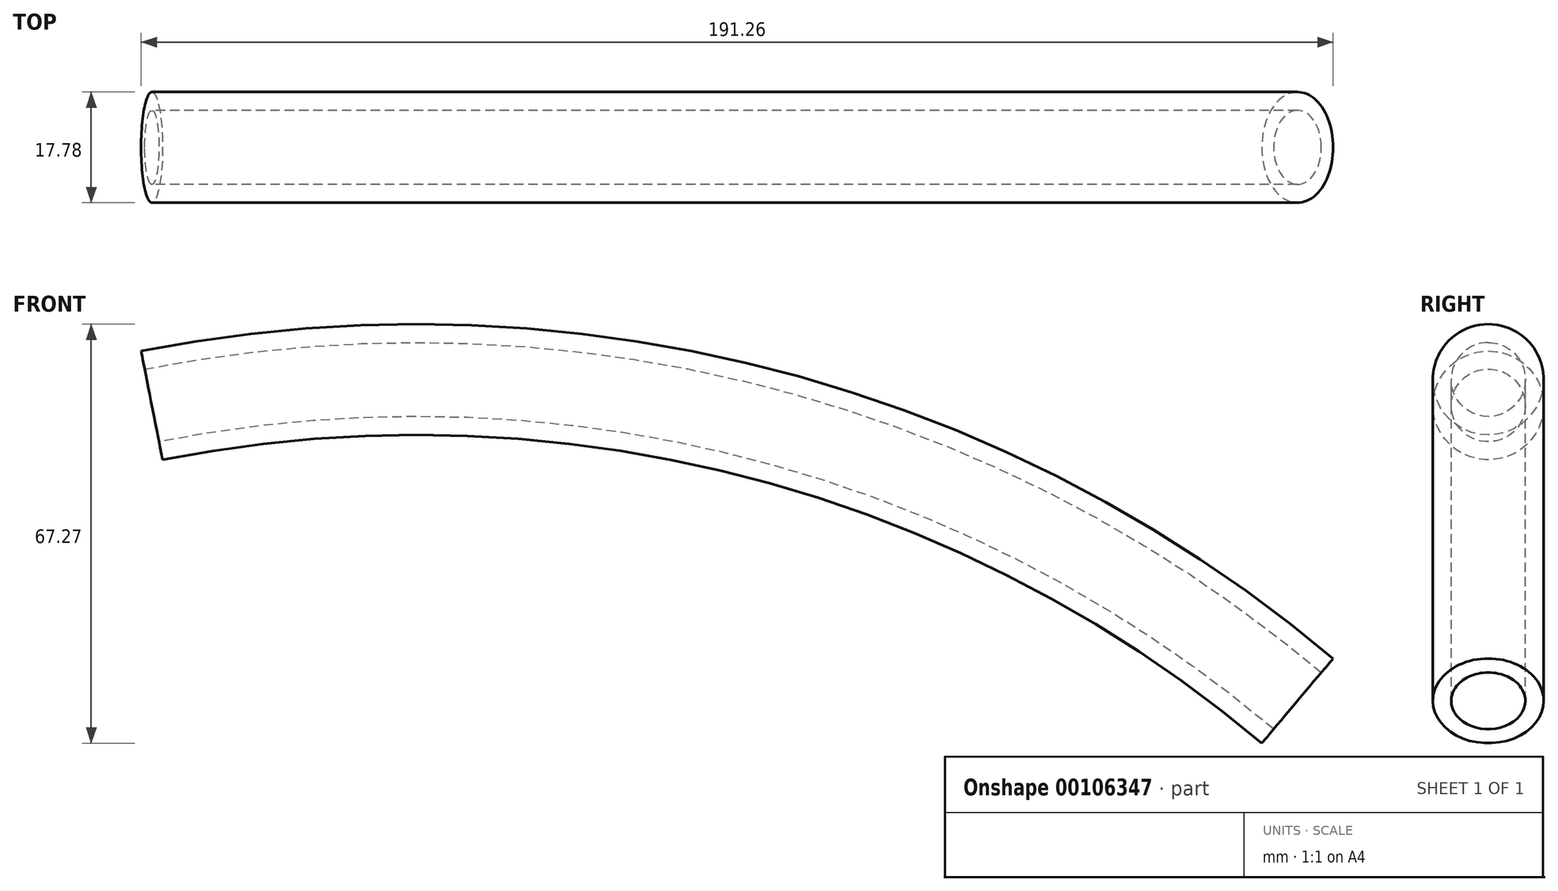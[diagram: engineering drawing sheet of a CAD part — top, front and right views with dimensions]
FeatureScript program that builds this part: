
annotation { "Feature Type Name" : "Feature", "Feature Type Description" : "" }
export const myFeature = defineFeature(function(context is Context, id is Id, definition is map)
    precondition{}
    {
        {
            var Q0;
            Q0=qCreatedBy(makeId("Front.planeOp"),FACE);
            var sketch = newSketch(context, id + "F0", { "sketchPlane" : qUnion([Q0])});
            skCircle(sketch, "E0", {"center": v(0, 0) * mm, "radius": 165.1 * mm});
            skLineSegment(sketch, "E1", {"start": v(-7.63, 164.92) * mm, "end": v(-208.53, 164.92) * mm});
            skLineSegment(sketch, "E2", {"start": v(127.2, -105.26) * mm, "end": v(67.26, -240.65) * mm});
            skLineSegment(sketch, "E3", {"start": v(-43.18, -159.35) * mm, "end": v(-100.79, -183.62) * mm});
            skLineSegment(sketch, "E4", {"start": v(-100.79, -183.62) * mm, "end": v(67.26, -240.65) * mm});
            skLineSegment(sketch, "E5", {"start": v(0, 0) * mm, "end": v(-133.18, -97.57) * mm});
            skLineSegment(sketch, "E6", {"start": v(-7.63, 164.92) * mm, "end": v(-24.71, 117.5) * mm});
            skLineSegment(sketch, "E7", {"start": v(-93.53, 164.92) * mm, "end": v(-24.71, 117.5) * mm});
            skLineSegment(sketch, "E8", {"start": v(-24.71, 117.5) * mm, "end": v(125.92, -15.38) * mm});
            skLineSegment(sketch, "E9", {"start": v(125.92, -15.38) * mm, "end": v(139.49, 0) * mm});
            skLineSegment(sketch, "E10", {"start": v(139.49, 0) * mm, "end": v(55.12, 74.42) * mm});
            skLineSegment(sketch, "E11", {"start": v(56.44, 75.91) * mm, "end": v(0, 0) * mm});
            skLineSegment(sketch, "E12", {"start": v(-225.74, 161.53) * mm, "end": v(-208.53, 164.92) * mm});
            skArc(sketch, "E13", {"start": v(-208.53, 164.92) * mm, "mid": v(-111.23, 162.12) * mm, "end": v(-24.71, 117.5) * mm});
            skLineSegment(sketch, "E14", {"start": v(42.97, 57.8) * mm, "end": v(125.92, -15.38) * mm});
            skArc(sketch, "E15", {"start": v(125.92, -15.38) * mm, "mid": v(140.4, -14.47) * mm, "end": v(139.49, 0) * mm});
            skLineSegment(sketch, "E16", {"start": v(139.49, 0) * mm, "end": v(70.33, 61) * mm});
            skArc(sketch, "E17", {"start": v(70.33, 61) * mm, "mid": v(55.93, 65.5) * mm, "end": v(42.97, 57.8) * mm});
            skLineSegment(sketch, "E18", {"start": v(-100.79, -183.62) * mm, "end": v(-218.73, -201.07) * mm});
            skLineSegment(sketch, "E19", {"start": v(-218.73, -201.07) * mm, "end": v(97.8, -391.34) * mm});
            skLineSegment(sketch, "E20", {"start": v(97.8, -391.34) * mm, "end": v(67.26, -240.65) * mm});
            skLineSegment(sketch, "E21", {"start": v(-208.53, 164.92) * mm, "end": v(-201.26, 128.08) * mm});
            skLineSegment(sketch, "E22", {"start": v(0, 0) * mm, "end": v(-84.51, -61.92) * mm});
            skLineSegment(sketch, "E23", {"start": v(42.97, 57.8) * mm, "end": v(31.67, 42.6) * mm});
            skArc(sketch, "E24", {"start": v(31.67, 42.6) * mm, "mid": v(-21.2, -15.46) * mm, "end": v(-84.51, -61.92) * mm});
            skArc(sketch, "E25", {"start": v(-84.51, -61.92) * mm, "mid": v(-155.37, -57.76) * mm, "end": v(-164.62, 12.61) * mm});
            skLineSegment(sketch, "E26", {"start": v(-172.71, -10.15) * mm, "end": v(-156.43, 52.8) * mm});
            skArc(sketch, "E27", {"start": v(-156.43, 52.8) * mm, "mid": v(-101.6, 134.85) * mm, "end": v(-7.63, 164.92) * mm});
            skArc(sketch, "E28", {"start": v(-7.63, 164.92) * mm, "mid": v(85.25, 138.66) * mm, "end": v(150.6, 67.64) * mm});
            skArc(sketch, "E29", {"start": v(150.6, 67.64) * mm, "mid": v(165.78, -22.45) * mm, "end": v(127.2, -105.26) * mm});
            skLineSegment(sketch, "E30", {"start": v(-24.71, 117.5) * mm, "end": v(-53.87, 84.44) * mm});
            skLineSegment(sketch, "E31", {"start": v(-31.88, 123.28) * mm, "end": v(-22.87, 148.3) * mm});
            skArc(sketch, "E32", {"start": v(-53.87, 84.44) * mm, "mid": v(-93.25, -7.7) * mm, "end": v(-70.03, -105.18) * mm});
            skArc(sketch, "E33", {"start": v(-70.03, -105.18) * mm, "mid": v(34.22, -154.86) * mm, "end": v(122.42, -80.3) * mm});
            skArc(sketch, "E34", {"start": v(122.42, -80.3) * mm, "mid": v(130.41, -50.94) * mm, "end": v(136.63, -21.14) * mm});
            skArc(sketch, "E35", {"start": v(136.63, -21.14) * mm, "mid": v(115.5, 72.32) * mm, "end": v(33.94, 122.63) * mm});
            skArc(sketch, "E36", {"start": v(-22.87, 148.3) * mm, "mid": v(-20.33, 153.28) * mm, "end": v(-16.66, 157.5) * mm});
            skArc(sketch, "E37", {"start": v(-16.66, 157.5) * mm, "mid": v(19.6, 155.27) * mm, "end": v(16.9, 119.05) * mm});
            skArc(sketch, "E38", {"start": v(16.9, 119.05) * mm, "mid": v(-0.44, 113.2) * mm, "end": v(-17.04, 120.9) * mm});
            skArc(sketch, "E39", {"start": v(-17.04, 120.9) * mm, "mid": v(-20.55, 129.68) * mm, "end": v(-17.15, 138.49) * mm});
            skArc(sketch, "E40", {"start": v(-17.15, 138.49) * mm, "mid": v(1.14, 144.5) * mm, "end": v(15.84, 132.06) * mm});
            skArc(sketch, "E41", {"start": v(15.84, 132.06) * mm, "mid": v(23.09, 123.88) * mm, "end": v(33.94, 122.63) * mm});
            skSolve(sketch);
        }
        {
            var Q0;
            Q0=sQuery(id+"F0.wireOp",EDGE,"E21");
            cPlane(context, id + "F1", {"entities" : qUnion([Q0]), "cplaneType" : CPlaneType.LINE_ANGLE, "offset" : 25.4 * mm, "angle" : 0 * degree, "width" : 152.4 * mm, "height" : 152.4 * mm});
        }
        {
            var Q0;
            Q0=qCreatedBy(id+"F1.planeOp",FACE);
            var sketch = newSketch(context, id + "F2", { "sketchPlane" : qUnion([Q0])});
            skCircle(sketch, "E42", {"center": v(0, 202.17) * mm, "radius": 5.94 * mm});
            skCircle(sketch, "E43", {"center": v(0, 202.17) * mm, "radius": 8.9 * mm});
            skSolve(sketch);
        }
        {
            var Q0;
            Q0=makeQuery(id+"F2.imprint","IMPRINT",FACE,{"disambiguationData":[TD([[makeQuery(id+"F2.imprint","IMPRINT",EDGE,{"derivedFrom":sQuery(id+"F2.wireOp",EDGE,"E42")}),-1.0]])]});
            var Q1;
            Q1=sQuery(id+"F0.wireOp",EDGE,"E13");
            sweep(context, id + "F3", {"profiles" : qUnion([Q0]), "path" : qUnion([Q1])});
        }
    });
